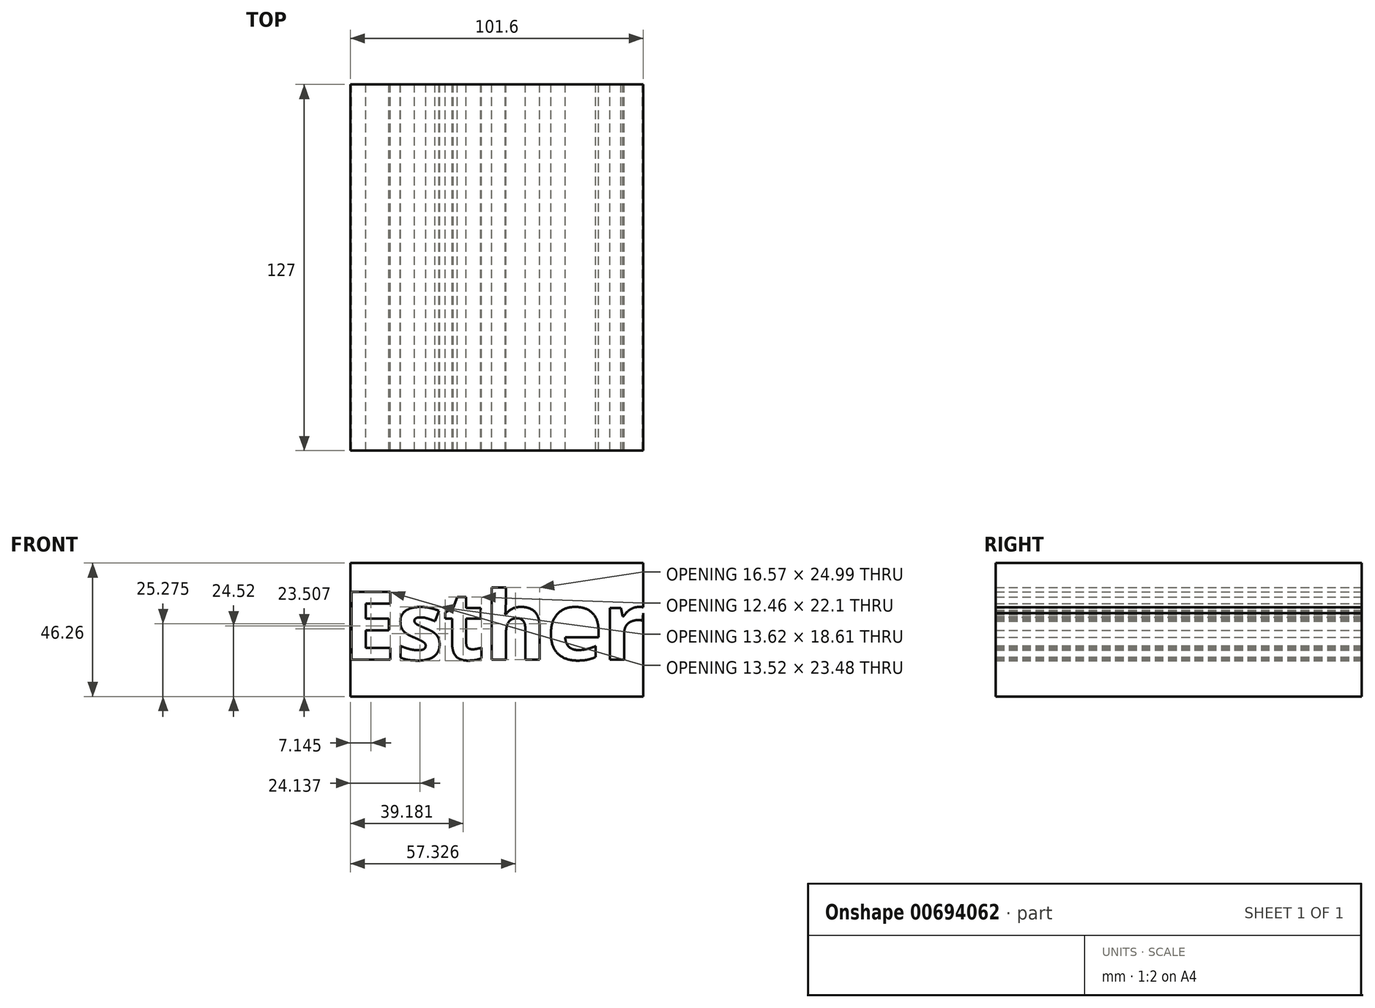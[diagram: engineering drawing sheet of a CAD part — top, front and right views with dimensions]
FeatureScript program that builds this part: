
annotation { "Feature Type Name" : "Feature", "Feature Type Description" : "" }
export const myFeature = defineFeature(function(context is Context, id is Id, definition is map)
    precondition{}
    {
        {
            var Q0;
            Q0=qCreatedBy(makeId("Front.planeOp"),FACE);
            var sketch = newSketch(context, id + "F0", { "sketchPlane" : qUnion([Q0])});
            skLineSegment(sketch, "E0.bottom", {"start": v(50.8, 23.13) * mm, "end": v(-50.8, 23.13) * mm});
            skLineSegment(sketch, "E0.top", {"start": v(50.8, -23.13) * mm, "end": v(-50.8, -23.13) * mm});
            skLineSegment(sketch, "E0.left", {"start": v(50.8, 23.13) * mm, "end": v(50.8, -23.13) * mm});
            skLineSegment(sketch, "E0.right", {"start": v(-50.8, 23.13) * mm, "end": v(-50.8, -23.13) * mm});
            skPoint(sketch, "E0.middle", {"position": v(0, 0) * mm});
            skText(sketch, "E1", { "text": "Esther", "fontName": "OpenSans-Bold.ttf"});
            const initialGuessF0  = {"E1": [-0.05337, -0.01035, 1, 0, 0.02368]};
            skSetInitialGuess(sketch, initialGuessF0);
            skSolve(sketch);
        }
        {
            var Q0;
            {var subQ7=sQuery(id+"F0.wireOp",EDGE,"E0.bottom");Q0=makeQuery(id+"F0.imprint","IMPRINT",FACE,{"disambiguationData":[TD([[makeQuery(id+"F0.imprint","IMPRINT",EDGE,{"derivedFrom":subQ7}),1.0]])]});}
            extrude(context, id + "F1", {"entities" : qUnion([Q0]), "depth" : 127 * mm, "offsetDistance" : 25.4 * mm});
        }
    });
